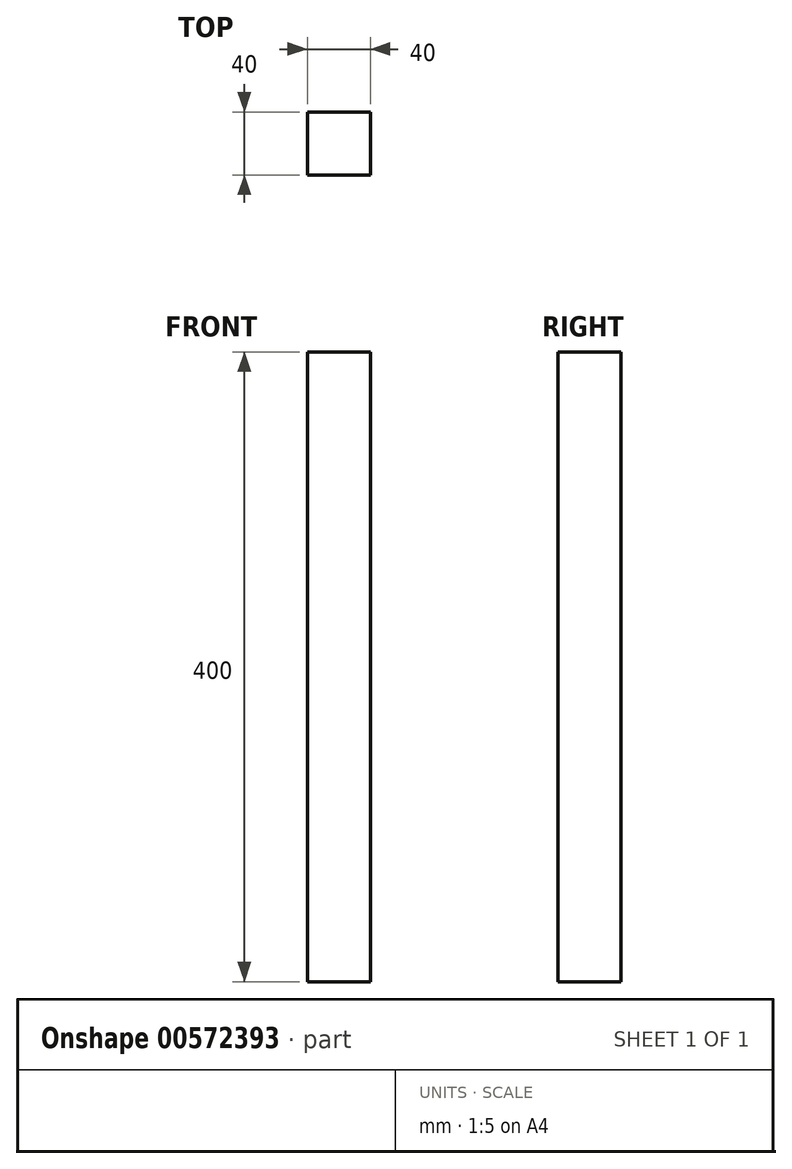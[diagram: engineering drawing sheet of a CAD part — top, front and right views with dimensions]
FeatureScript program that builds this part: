
annotation { "Feature Type Name" : "Feature", "Feature Type Description" : "" }
export const myFeature = defineFeature(function(context is Context, id is Id, definition is map)
    precondition{}
    {
        {
            var Q0;
            Q0=qCreatedBy(makeId("Top.planeOp"),FACE);
            var sketch = newSketch(context, id + "F0", { "sketchPlane" : qUnion([Q0])});
            skLineSegment(sketch, "E0.bottom", {"start": v(-40, 40) * mm, "end": v(0, 40) * mm});
            skLineSegment(sketch, "E0.top", {"start": v(-40, 0) * mm, "end": v(0, 0) * mm});
            skLineSegment(sketch, "E0.left", {"start": v(-40, 40) * mm, "end": v(-40, 0) * mm});
            skLineSegment(sketch, "E0.right", {"start": v(0, 40) * mm, "end": v(0, 0) * mm});
            skSolve(sketch);
        }
        {
            var Q0;
            Q0 = qSketchRegion(id + "F0", true);
            extrude(context, id + "F1", {"entities" : qUnion([Q0]), "depth" : 400 * mm, "offsetDistance" : 25 * mm});
        }
    });
